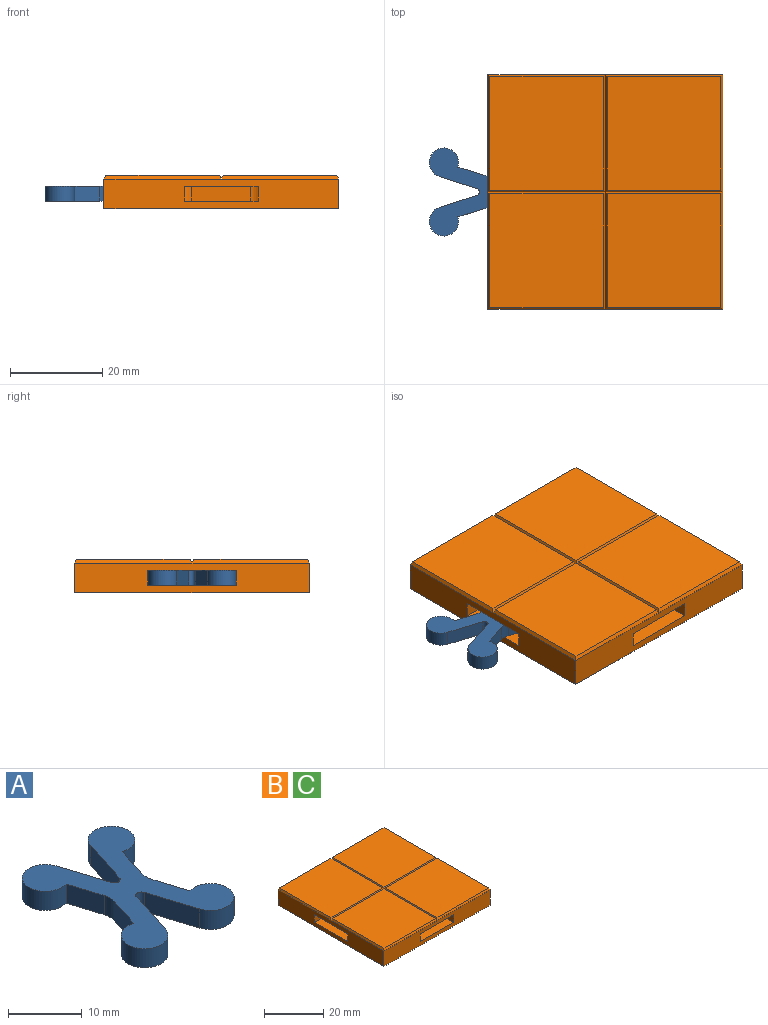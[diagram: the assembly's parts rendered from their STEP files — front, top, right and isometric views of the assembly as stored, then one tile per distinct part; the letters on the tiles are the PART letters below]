
ASSEMBLY  parts=3 mates=1
PART A: 18 faces, bbox 19.1x25.4x3.2 mm
  f0: cylinder r=3.17mm len=3.18mm, axis (0,0,-1), area 6.2mm2, adj f1,f15,f16,f17
  f1: plane 5.54x3.18mm, normal (-0.95,0.3,0), area 18.4mm2, adj f0,f2,f16,f17
  f2: cylinder r=3.17mm len=6.35mm, axis (0,0,-1), area 47.5mm2, adj f1,f3,f16,f17
  f3: plane 8.1x3.18mm, normal (0.95,-0.3,0), area 27mm2, adj f2,f4,f16,f17
  f4: cylinder r=0.79mm len=3.18mm, axis (0,0,-1), area 6.4mm2, adj f3,f5,f16,f17
  f5: plane 8.1x3.18mm, normal (-0.95,-0.3,0), area 27mm2, adj f4,f6,f16,f17
  f6: cylinder r=3.17mm len=6.35mm, axis (0,0,-1), area 47.5mm2, adj f5,f7,f16,f17
  f7: plane 5.54x3.18mm, normal (0.95,0.3,0), area 18.4mm2, adj f6,f8,f16,f17
  f8: cylinder r=3.17mm len=3.18mm, axis (0,0,-1), area 6.2mm2, adj f7,f9,f16,f17
  f9: plane 5.54x3.18mm, normal (0.95,-0.3,0), area 18.4mm2, adj f8,f10,f16,f17
  f10: cylinder r=3.17mm len=6.35mm, axis (0,0,-1), area 47.5mm2, adj f9,f11,f16,f17
  f11: plane 8.1x3.18mm, normal (-0.95,0.3,0), area 27mm2, adj f10,f12,f16,f17
  f12: cylinder r=0.79mm len=3.18mm, axis (0,0,-1), area 6.4mm2, adj f11,f13,f16,f17
  f13: plane 8.1x3.18mm, normal (0.95,0.3,0), area 27mm2, adj f12,f14,f16,f17
  f14: cylinder r=3.17mm len=6.35mm, axis (0,0,-1), area 47.5mm2, adj f13,f15,f16,f17
  f15: plane 5.54x3.18mm, normal (-0.95,-0.3,0), area 18.4mm2, adj f0,f14,f16,f17
  f16: plane 25.4x19.05mm, normal (0,0,1), area 230.9mm2, adj f0,f1,f2,f3,f4,f5,f6,f7
  f17: plane 25.4x19.05mm, normal (0,0,-1), area 230.9mm2, adj f0,f1,f2,f3,f4,f5,f6,f7
PART B: 82 faces, bbox 50.8x50.8x7.1 mm
  f0: cylinder r=3.17mm len=5.92mm, axis (0,0,-1), area 26.4mm2, adj f1,f23,f27,f31
  f1: plane 12.7x3.18mm, normal (0,-1,0), area 40.3mm2, adj f0,f2,f27,f31
  f2: cylinder r=3.17mm len=5.92mm, axis (0,0,-1), area 26.4mm2, adj f1,f3,f27,f31
  f3: plane 6.78x3.18mm, normal (-1,0,0), area 21.5mm2, adj f2,f22,f27,f31
  f4: plane 6.78x3.18mm, normal (0,1,0), area 21.5mm2, adj f5,f9,f24,f30
  f5: cylinder r=3.17mm len=5.92mm, axis (0,0,-1), area 26.4mm2, adj f4,f6,f24,f30
  f6: plane 12.7x3.18mm, normal (1,0,0), area 40.3mm2, adj f5,f7,f24,f30
  f7: cylinder r=3.17mm len=5.92mm, axis (0,0,-1), area 26.4mm2, adj f6,f8,f24,f30
  f8: plane 6.78x3.18mm, normal (0,-1,0), area 21.5mm2, adj f7,f9,f24,f30
  f9: plane 50.8x6.35mm, normal (1,0,0), area 272.2mm2, adj f4,f8,f15,f22,f24,f30,f32,f66
  f10: plane 6.78x3.18mm, normal (-1,0,0), area 21.5mm2, adj f11,f15,f25,f29
  f11: cylinder r=3.17mm len=5.92mm, axis (0,0,-1), area 26.4mm2, adj f10,f12,f25,f29
  f12: plane 12.7x3.18mm, normal (0,1,0), area 40.3mm2, adj f11,f13,f25,f29
  f13: cylinder r=3.17mm len=5.92mm, axis (0,0,-1), area 26.4mm2, adj f12,f14,f25,f29
  f14: plane 6.78x3.18mm, normal (1,0,0), area 21.5mm2, adj f13,f15,f25,f29
  f15: plane 50.8x6.35mm, normal (0,1,0), area 272.2mm2, adj f9,f10,f14,f21,f25,f29,f32,f75
  f16: plane 6.78x3.18mm, normal (0,-1,0), area 21.5mm2, adj f17,f21,f26,f28
  f17: cylinder r=3.17mm len=5.92mm, axis (0,0,-1), area 26.4mm2, adj f16,f18,f26,f28
  f18: plane 12.7x3.18mm, normal (-1,0,0), area 40.3mm2, adj f17,f19,f26,f28
  f19: cylinder r=3.17mm len=5.92mm, axis (0,0,-1), area 26.4mm2, adj f18,f20,f26,f28
  f20: plane 6.78x3.18mm, normal (0,1,0), area 21.5mm2, adj f19,f21,f26,f28
  f21: plane 50.8x6.35mm, normal (-1,0,0), area 272.2mm2, adj f15,f16,f20,f22,f26,f28,f32,f68
  f22: plane 50.8x6.35mm, normal (0,-1,0), area 272.2mm2, adj f3,f9,f21,f23,f27,f31,f32,f64
  f23: plane 6.78x3.18mm, normal (1,0,0), area 21.5mm2, adj f0,f22,f27,f31
  f24: plane 19.05x12.7mm, normal (0,0,-1), area 213.6mm2, adj f4,f5,f6,f7,f8,f9
  f25: plane 19.05x12.7mm, normal (0,0,-1), area 213.6mm2, adj f10,f11,f12,f13,f14,f15
  f26: plane 19.05x12.7mm, normal (0,0,-1), area 213.6mm2, adj f16,f17,f18,f19,f20,f21
  f27: plane 19.05x12.7mm, normal (0,0,-1), area 213.6mm2, adj f0,f1,f2,f3,f22,f23
  f28: plane 19.05x12.7mm, normal (0,0,1), area 213.6mm2, adj f16,f17,f18,f19,f20,f21
  f29: plane 19.05x12.7mm, normal (0,0,1), area 213.6mm2, adj f10,f11,f12,f13,f14,f15
  f30: plane 19.05x12.7mm, normal (0,0,1), area 213.6mm2, adj f4,f5,f6,f7,f8,f9
  f31: plane 19.05x12.7mm, normal (0,0,1), area 213.6mm2, adj f0,f1,f2,f3,f22,f23
  f32: plane 50.8x50.8mm, normal (0,0,-1), area 1781.8mm2, adj f9,f15,f21,f22,f34,f35,f36,f37
  f33: plane 44.45x44.45mm, normal (0,0,-1), area 798.8mm2, adj f34,f35,f36,f37,f38,f39,f40,f41
  f34: cylinder r=6.35mm len=10.55mm, axis (0,0,-1), area 69.4mm2, adj f32,f33,f35,f61
  f35: plane 4.76x2.15mm, normal (0,1,0), area 10.2mm2, adj f32,f33,f34,f36
  f36: plane 11.11x4.76mm, normal (1,0,0), area 52.9mm2, adj f32,f33,f35,f37
  f37: plane 11.11x4.76mm, normal (0,-1,0), area 52.9mm2, adj f32,f33,f36,f38
  f38: plane 4.76x2.15mm, normal (-1,0,0), area 10.2mm2, adj f32,f33,f37,f39
  f39: cylinder r=6.35mm len=10.55mm, axis (0,0,-1), area 69.4mm2, adj f32,f33,f38,f40
  f40: plane 12.7x4.76mm, normal (0,-1,0), area 60.5mm2, adj f32,f33,f39,f41
  f41: cylinder r=6.35mm len=10.55mm, axis (0,0,-1), area 69.4mm2, adj f32,f33,f40,f42
  f42: plane 4.76x2.15mm, normal (1,0,0), area 10.2mm2, adj f32,f33,f41,f43
  f43: plane 11.11x4.76mm, normal (0,-1,0), area 52.9mm2, adj f32,f33,f42,f44
  f44: plane 11.11x4.76mm, normal (-1,0,0), area 52.9mm2, adj f32,f33,f43,f45
  f45: plane 4.76x2.15mm, normal (0,1,0), area 10.2mm2, adj f32,f33,f44,f46
  f46: cylinder r=6.35mm len=10.55mm, axis (0,0,-1), area 69.4mm2, adj f32,f33,f45,f47
  f47: plane 12.7x4.76mm, normal (-1,0,0), area 60.5mm2, adj f32,f33,f46,f48
  f48: cylinder r=6.35mm len=10.55mm, axis (0,0,-1), area 69.4mm2, adj f32,f33,f47,f49
  f49: plane 4.76x2.15mm, normal (0,-1,0), area 10.2mm2, adj f32,f33,f48,f50
  f50: plane 11.11x4.76mm, normal (-1,0,0), area 52.9mm2, adj f32,f33,f49,f51
  f51: plane 11.11x4.76mm, normal (0,1,0), area 52.9mm2, adj f32,f33,f50,f52
  f52: plane 4.76x2.15mm, normal (1,0,0), area 10.2mm2, adj f32,f33,f51,f53
  f53: cylinder r=6.35mm len=10.55mm, axis (0,0,-1), area 69.4mm2, adj f32,f33,f52,f54
  f54: plane 12.7x4.76mm, normal (0,1,0), area 60.5mm2, adj f32,f33,f53,f55
  f55: cylinder r=6.35mm len=10.55mm, axis (0,0,-1), area 69.4mm2, adj f32,f33,f54,f56
  f56: plane 4.76x2.15mm, normal (-1,0,0), area 10.2mm2, adj f32,f33,f55,f57
  f57: plane 11.11x4.76mm, normal (0,1,0), area 52.9mm2, adj f32,f33,f56,f58
  f58: plane 11.11x4.76mm, normal (1,0,0), area 52.9mm2, adj f32,f33,f57,f59
  f59: plane 4.76x2.15mm, normal (0,-1,0), area 10.2mm2, adj f32,f33,f58,f60
  f60: cylinder r=6.35mm len=10.55mm, axis (0,0,-1), area 69.4mm2, adj f32,f33,f59,f61
  f61: plane 12.7x4.76mm, normal (1,0,0), area 60.5mm2, adj f32,f33,f34,f60
  f62: plane 24.61x24.61mm, normal (0,0,1), area 605.5mm2, adj f63,f64,f65,f66
  f63: plane 25.4x0.79mm, normal (-0.89,0,0.45), area 22.2mm2, adj f62,f64,f65,f71
  f64: plane 25.4x0.79mm, normal (0,-0.89,0.45), area 22.2mm2, adj f22,f62,f63,f66
  f65: plane 25.4x0.79mm, normal (0,0.89,0.45), area 22.2mm2, adj f62,f63,f66,f74
  f66: plane 25.4x0.79mm, normal (0.89,0,0.45), area 22.2mm2, adj f9,f62,f64,f65
  f67: plane 24.61x24.61mm, normal (0,0,1), area 605.5mm2, adj f68,f69,f70,f71
  f68: plane 25.4x0.79mm, normal (-0.89,0,0.45), area 22.2mm2, adj f21,f67,f69,f70
  f69: plane 25.4x0.79mm, normal (0,-0.89,0.45), area 22.2mm2, adj f22,f67,f68,f71
  f70: plane 25.4x0.79mm, normal (0,0.89,0.45), area 22.2mm2, adj f67,f68,f71,f79
  f71: plane 25.4x0.79mm, normal (0.89,0,0.45), area 22.2mm2, adj f63,f67,f69,f70
  f72: plane 24.61x24.61mm, normal (0,0,1), area 605.5mm2, adj f73,f74,f75,f76
  f73: plane 25.4x0.79mm, normal (-0.89,0,0.45), area 22.2mm2, adj f72,f74,f75,f81
  f74: plane 25.4x0.79mm, normal (0,-0.89,0.45), area 22.2mm2, adj f65,f72,f73,f76
  f75: plane 25.4x0.79mm, normal (0,0.89,0.45), area 22.2mm2, adj f15,f72,f73,f76
  f76: plane 25.4x0.79mm, normal (0.89,0,0.45), area 22.2mm2, adj f9,f72,f74,f75
  f77: plane 24.61x24.61mm, normal (0,0,1), area 605.5mm2, adj f78,f79,f80,f81
  f78: plane 25.4x0.79mm, normal (-0.89,0,0.45), area 22.2mm2, adj f21,f77,f79,f80
  f79: plane 25.4x0.79mm, normal (0,-0.89,0.45), area 22.2mm2, adj f70,f77,f78,f81
  f80: plane 25.4x0.79mm, normal (0,0.89,0.45), area 22.2mm2, adj f15,f77,f78,f81
  f81: plane 25.4x0.79mm, normal (0.89,0,0.45), area 22.2mm2, adj f73,f77,f79,f80
PART C: same geometry as B
PLACE A rot(axis=(0,0,-1),90deg) t=(-9.43,-12.01,-0.86)mm
PLACE B t=(15.97,-12.01,-0.86)mm
PLACE C t=(15.97,-12.01,-0.86)mm
MATE cylindrical A.f14 <-> C.f17  axis (0,0,-1) through (0.09,-5.66,-0.86)mm
